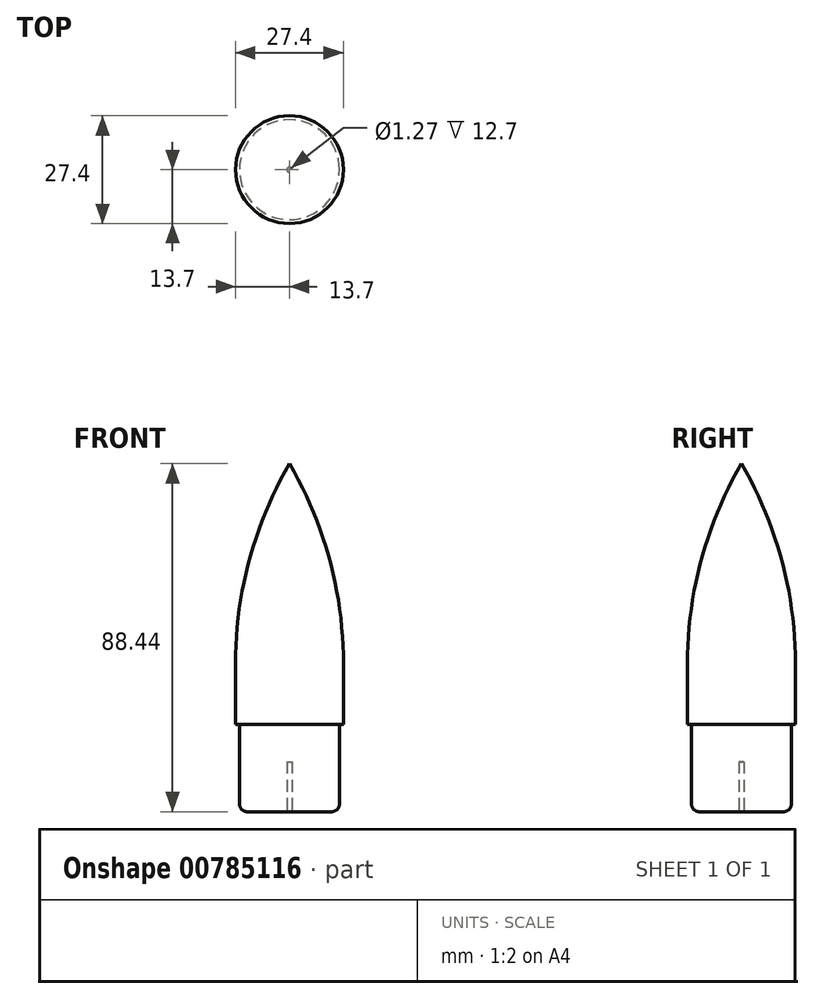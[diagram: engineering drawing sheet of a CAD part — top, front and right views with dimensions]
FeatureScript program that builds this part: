
annotation { "Feature Type Name" : "Feature", "Feature Type Description" : "" }
export const myFeature = defineFeature(function(context is Context, id is Id, definition is map)
    precondition{}
    {
        {
            var Q0;
            Q0=qCreatedBy(makeId("Front.planeOp"),FACE);
            var sketch = newSketch(context, id + "F0", { "sketchPlane" : qUnion([Q0])});
            skLineSegment(sketch, "E0", {"start": v(0, 0) * mm, "end": v(0, 88.44) * mm});
            skArc(sketch, "E1", {"start": v(13.7, 37.64) * mm, "mid": v(10.21, 63.95) * mm, "end": v(0, 88.44) * mm});
            skLineSegment(sketch, "E2", {"start": v(13.7, 37.64) * mm, "end": v(13.7, 22.14) * mm});
            skLineSegment(sketch, "E3", {"start": v(0, 0) * mm, "end": v(12.7, 0) * mm});
            skLineSegment(sketch, "E4", {"start": v(13.7, 22.14) * mm, "end": v(12.7, 22.14) * mm});
            skLineSegment(sketch, "E5", {"start": v(12.7, 22.14) * mm, "end": v(12.7, 0) * mm});
            skLineSegment(sketch, "E6", {"start": v(0, 0) * mm, "end": v(0, -7.7) * mm, "construction": true});
            skSolve(sketch);
        }
        {
            var Q0;
            Q0=makeQuery(id+"F0.imprint","IMPRINT",FACE,{"disambiguationData":[TD([[makeQuery(id+"F0.imprint","IMPRINT",EDGE,{"derivedFrom":sQuery(id+"F0.wireOp",EDGE,"E0")}),-1.0]])]});
            var Q1;
            Q1=sQuery(id+"F0.wireOp",EDGE,"E6");
            revolve(context, id + "F1", {"surfaceOperationType" : NewSurfaceOperationType.NEW, "entities" : qUnion([Q0]), "axis" : qUnion([Q1]), "revolveType" : RevolveType.FULL});
        }
        {
            var Q0;
            Q0=makeQuery(id+"F1.opRevolve","SWEPT_FACE",FACE,{"disambiguationData":[OSD([sQuery(id+"F0.wireOp",EDGE,"E3")])]});
            var sketch = newSketch(context, id + "F2", { "sketchPlane" : qUnion([Q0])});
            skCircle(sketch, "E7", {"center": v(0, 0) * mm, "radius": 0.64 * mm});
            skSolve(sketch);
        }
        {
            var Q0;
            Q0=makeQuery(id+"F2.imprint","IMPRINT",FACE,{"disambiguationData":[TD([[makeQuery(id+"F2.imprint","IMPRINT",EDGE,{"derivedFrom":sQuery(id+"F2.wireOp",EDGE,"E7")}),1.0]])]});
            extrude(context, id + "F3", {"entities" : qUnion([Q0]), "operationType" : NewBodyOperationType.REMOVE, "oppositeDirection" : true, "depth" : 12.7 * mm, "offsetDistance" : 25.4 * mm});
        }
        {
            var Q0;
            Q0=makeQuery(id+"F1.opRevolve","SWEPT_EDGE",EDGE,{"disambiguationData":[OSD([sQuery(id+"F0.wireOp",EDGE,"E3"),sQuery(id+"F0.wireOp",EDGE,"E5")])]});
            fillet(context, id + "F4", {"entities" : qUnion([Q0]), "radius" : 2 * mm, "tangentPropagation" : true, "allowEdgeOverflow" : false});
        }
    });
